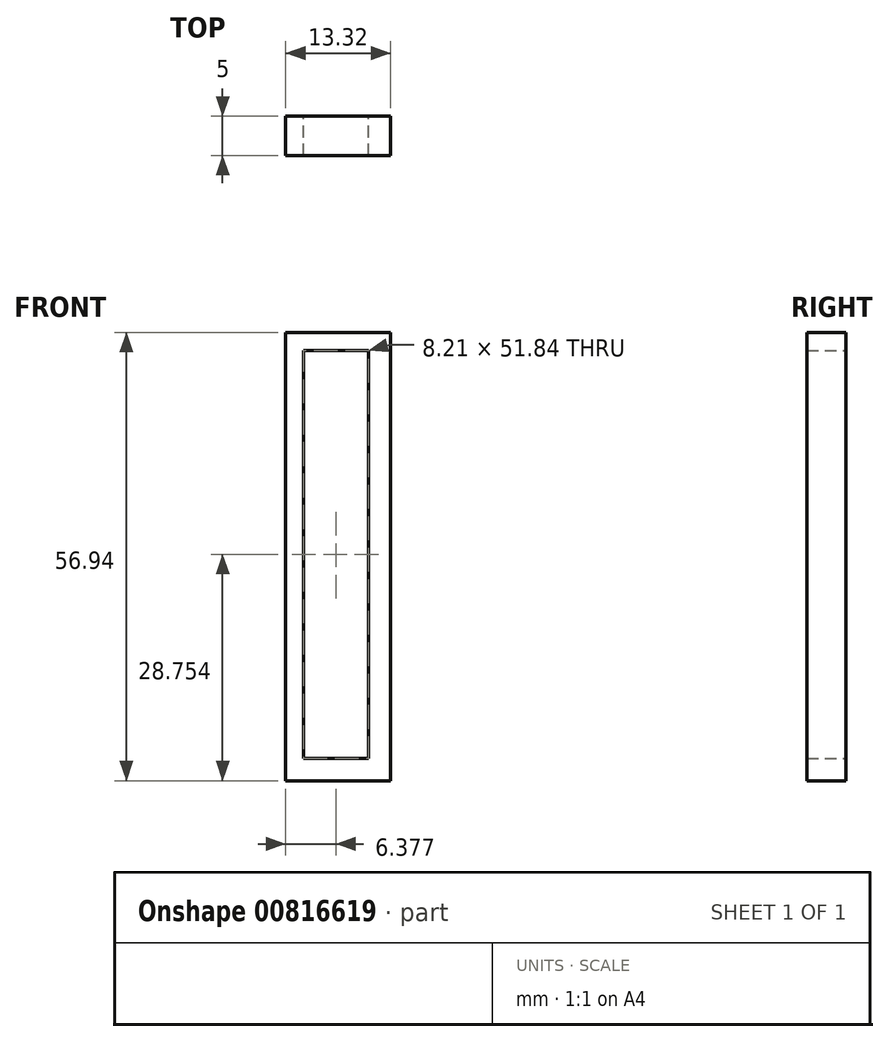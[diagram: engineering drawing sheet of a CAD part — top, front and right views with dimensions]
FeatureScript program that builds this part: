
annotation { "Feature Type Name" : "Feature", "Feature Type Description" : "" }
export const myFeature = defineFeature(function(context is Context, id is Id, definition is map)
    precondition{}
    {
        {
            var Q0;
            Q0=qCreatedBy(makeId("Front.planeOp"),FACE);
            var sketch = newSketch(context, id + "F0", { "sketchPlane" : qUnion([Q0])});
            skLineSegment(sketch, "E0.bottom", {"start": v(-6.66, 39.8) * mm, "end": v(6.66, 39.8) * mm});
            skLineSegment(sketch, "E0.top", {"start": v(-6.66, -17.14) * mm, "end": v(6.66, -17.14) * mm});
            skLineSegment(sketch, "E0.left", {"start": v(-6.66, 39.8) * mm, "end": v(-6.66, -17.14) * mm});
            skLineSegment(sketch, "E0.right", {"start": v(6.66, 39.8) * mm, "end": v(6.66, -17.14) * mm});
            skLineSegment(sketch, "E1.bottom", {"start": v(-4.4, 37.53) * mm, "end": v(3.82, 37.53) * mm});
            skLineSegment(sketch, "E1.top", {"start": v(-4.4, -14.3) * mm, "end": v(3.82, -14.3) * mm});
            skLineSegment(sketch, "E1.left", {"start": v(-4.4, 37.53) * mm, "end": v(-4.4, -14.3) * mm});
            skLineSegment(sketch, "E1.right", {"start": v(3.82, 37.53) * mm, "end": v(3.82, -14.3) * mm});
            skSolve(sketch);
        }
        {
            var Q0;
            Q0=makeQuery(id+"F0.imprint","IMPRINT",FACE,{"disambiguationData":[TD([[makeQuery(id+"F0.imprint","IMPRINT",EDGE,{"derivedFrom":sQuery(id+"F0.wireOp",EDGE,"E0.bottom")}),-1.0]])]});
            extrude(context, id + "F1", {"entities" : qUnion([Q0]), "depth" : 5 * mm, "offsetDistance" : 25 * mm});
        }
    });
